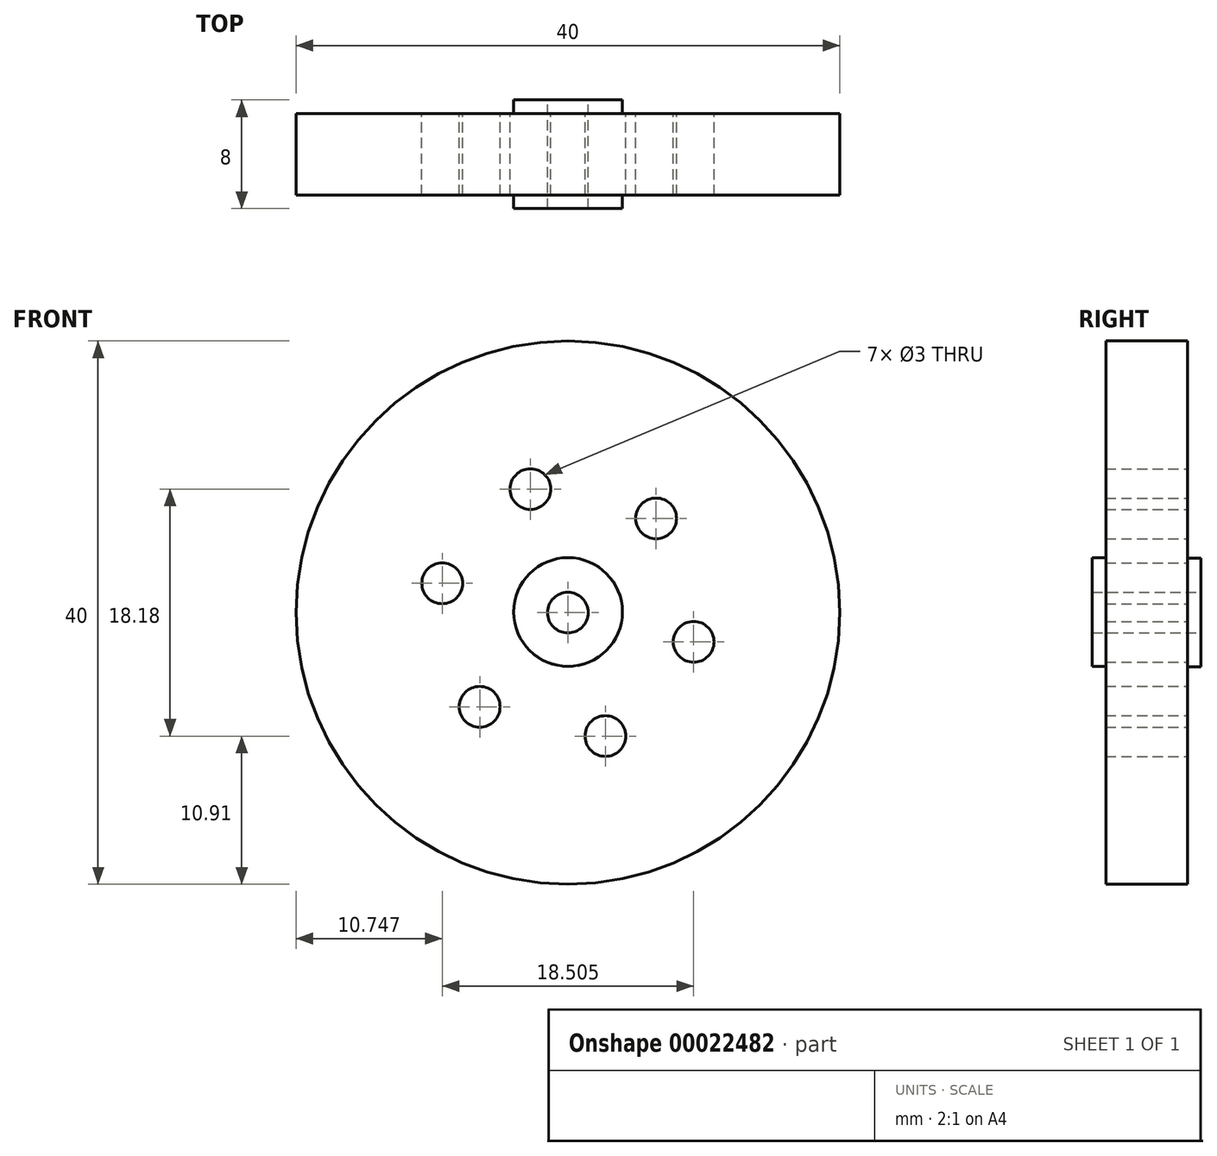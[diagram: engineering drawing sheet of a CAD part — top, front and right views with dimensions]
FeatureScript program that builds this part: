
annotation { "Feature Type Name" : "Feature", "Feature Type Description" : "" }
export const myFeature = defineFeature(function(context is Context, id is Id, definition is map)
    precondition{}
    {
        {
            var Q0;
            Q0=qCreatedBy(makeId("Front.planeOp"),FACE);
            var sketch = newSketch(context, id + "F0", { "sketchPlane" : qUnion([Q0])});
            skCircle(sketch, "E0", {"center": v(0, 0) * mm, "radius": 20 * mm});
            skCircle(sketch, "E1", {"center": v(0, 0) * mm, "radius": 4 * mm});
            skCircle(sketch, "E2", {"center": v(0, 0) * mm, "radius": 1.5 * mm});
            skCircle(sketch, "E3", {"center": v(6.5, 6.94) * mm, "radius": 1.5 * mm});
            skLineSegment(sketch, "E4.trimOffspring", {"start": v(6.5, 6.94) * mm, "end": v(7.52, 8.03) * mm});
            skCircle(sketch, "E5.1.0", {"center": v(-2.76, 9.09) * mm, "radius": 1.5 * mm});
            skCircle(sketch, "E5.2.0", {"center": v(-9.25, 2.15) * mm, "radius": 1.5 * mm});
            skCircle(sketch, "E5.3.0", {"center": v(-6.5, -6.94) * mm, "radius": 1.5 * mm});
            skCircle(sketch, "E5.4.0", {"center": v(2.76, -9.09) * mm, "radius": 1.5 * mm});
            skCircle(sketch, "E5.5.0", {"center": v(9.25, -2.15) * mm, "radius": 1.5 * mm});
            skPoint(sketch, "E6.orphan", {"position": v(0, 20) * mm});
            skLineSegment(sketch, "E7.trimOffspring", {"start": v(0, 0) * mm, "end": v(4, 0) * mm});
            skPoint(sketch, "E8.start.orphan", {"position": v(-20, 0) * mm});
            skSolve(sketch);
        }
        {
            var Q0;
            Q0 = qSketchRegion(id + "F0", true);
            var Q1;
            Q1=makeQuery(id+"F0.imprint","IMPRINT",FACE,{"disambiguationData":[TD([[makeQuery(id+"F0.imprint","IMPRINT",EDGE,{"derivedFrom":sQuery(id+"F0.wireOp",EDGE,"E1")}),1.0]])]});
            extrude(context, id + "F1", {"entities" : qUnion([Q0, Q1]), "depth" : 6 * mm});
        }
        {
            var Q0;
            Q0=makeQuery(id+"F1.opExtrude","CAP_FACE",FACE,{"disambiguationData":[OSD([sQuery(id+"F0.wireOp",EDGE,"E0"),sQuery(id+"F0.wireOp",EDGE,"E2"),sQuery(id+"F0.wireOp",EDGE,"E3"),sQuery(id+"F0.wireOp",EDGE,"E5.1.0"),sQuery(id+"F0.wireOp",EDGE,"E5.2.0"),sQuery(id+"F0.wireOp",EDGE,"E5.3.0"),sQuery(id+"F0.wireOp",EDGE,"E5.4.0"),sQuery(id+"F0.wireOp",EDGE,"E5.5.0")])],"isStart":false});
            var sketch = newSketch(context, id + "F2", { "sketchPlane" : qUnion([Q0])});
            skCircle(sketch, "E9", {"center": v(0, 0.04) * mm, "radius": 4 * mm});
            skSolve(sketch);
        }
        {
            var Q0;
            Q0=makeQuery(id+"F2.imprint","IMPRINT",FACE,{"disambiguationData":[TD([[makeQuery(id+"F2.imprint","IMPRINT",EDGE,{"derivedFrom":sQuery(id+"F2.wireOp",EDGE,"E9")}),1.0]])]});
            extrude(context, id + "F3", {"entities" : qUnion([Q0]), "operationType" : NewBodyOperationType.ADD, "depth" : 1 * mm});
        }
        {
            var Q0;
            Q0=makeQuery(id+"F0.imprint","IMPRINT",FACE,{"disambiguationData":[TD([[makeQuery(id+"F0.imprint","IMPRINT",EDGE,{"derivedFrom":sQuery(id+"F0.wireOp",EDGE,"E1")}),1.0]])]});
            extrude(context, id + "F4", {"entities" : qUnion([Q0]), "operationType" : NewBodyOperationType.ADD, "oppositeDirection" : true, "depth" : 1 * mm});
        }
    });
